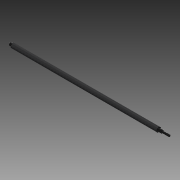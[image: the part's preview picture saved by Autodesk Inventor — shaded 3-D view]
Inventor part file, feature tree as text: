
AUTODESK INVENTOR PART (.ipt)
format: ipt  version: 2018 (Build 220112000, 112)  size: 132,608 bytes
history: native  units: mm
features: sketch x4, revolve x3, thread x1, extrude x1
ambient origin geometry x8: Origin, YZ Plane, XZ Plane, XY Plane, X Axis, Y Axis, Z Axis, Center Point
bodies: Solid1 (feature_tree)
feature tree (9):
  revolve  "Revolution1"  [1 undecoded]
  thread  "Thread1"  [1 undecoded]
  revolve  "Revolution2"  [1 undecoded]
  revolve  "Revolution3"  [1 undecoded]
  extrude  "Extrusion1"  [1 undecoded]
  sketch  "Sketch_16"
  sketch  "Sketch_23"
  sketch  "Sketch_4"  dims[d0=360.0deg d1=384.0mm d2=0.0mm d3=360.0deg]
  sketch  "Sketch_8"  dims[d4=360.0deg d5=7.0mm d6=0.0mm]
note: 5 required parameter values undecoded (feature->parameter linkage not recoverable at this tier; creation-order binding heuristic only, values carry confidence <= 0.55)